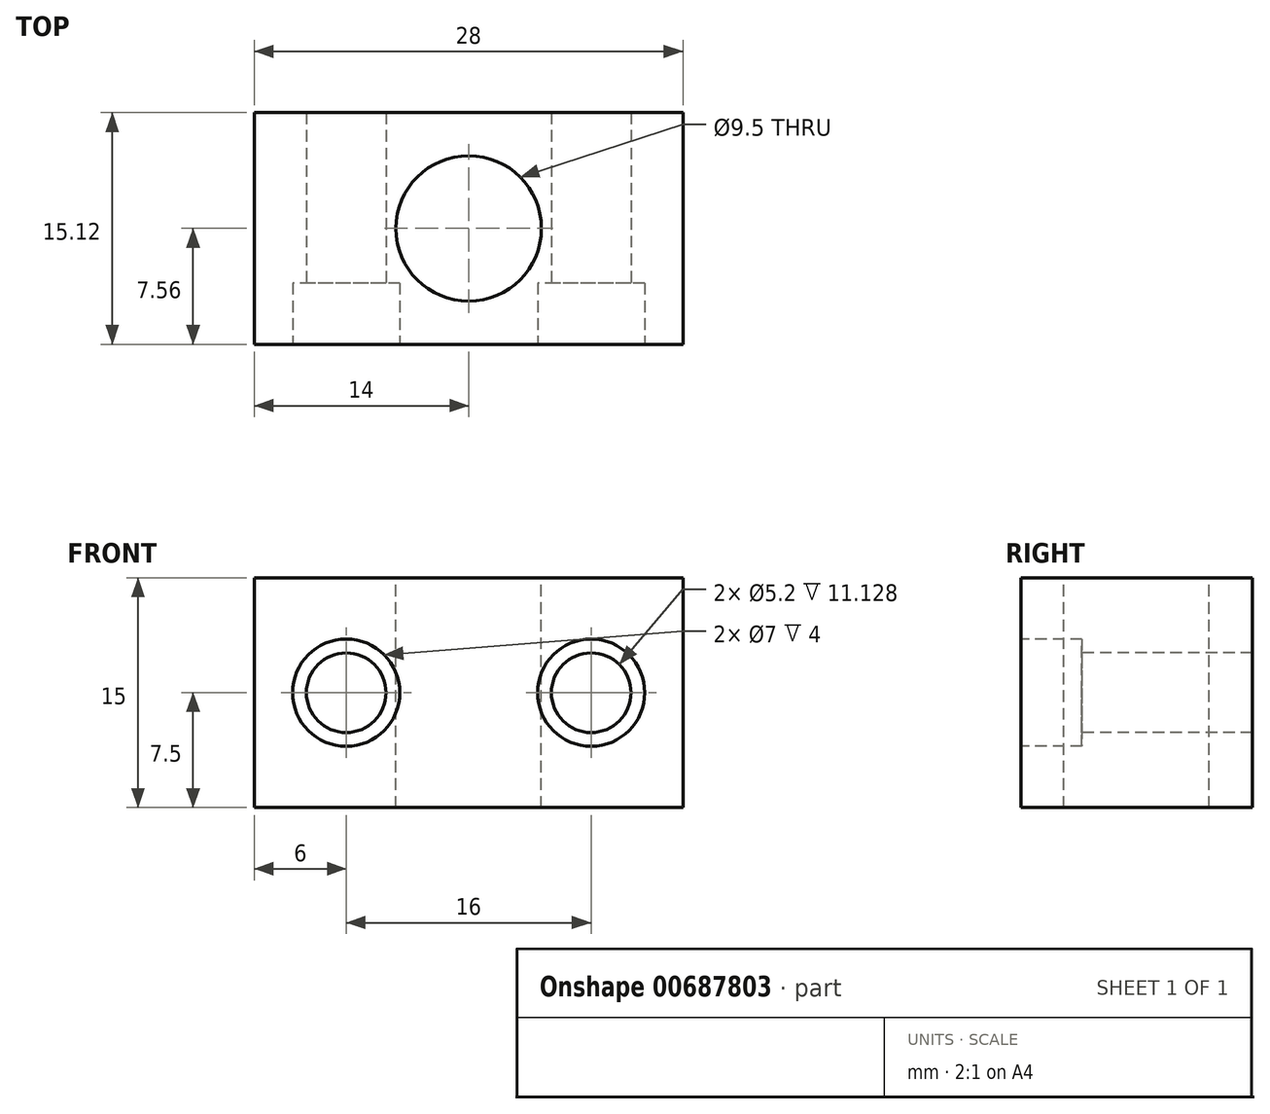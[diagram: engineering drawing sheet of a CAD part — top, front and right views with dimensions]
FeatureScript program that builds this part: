
annotation { "Feature Type Name" : "Feature", "Feature Type Description" : "" }
export const myFeature = defineFeature(function(context is Context, id is Id, definition is map)
    precondition{}
    {
        {
            var Q0;
            Q0=qCreatedBy(makeId("Top.planeOp"),FACE);
            var sketch = newSketch(context, id + "F0", { "sketchPlane" : qUnion([Q0])});
            skLineSegment(sketch, "E0.bottom", {"start": v(14, 7.56) * mm, "end": v(-14, 7.56) * mm});
            skLineSegment(sketch, "E0.top", {"start": v(14, -7.56) * mm, "end": v(-14, -7.56) * mm});
            skLineSegment(sketch, "E0.left", {"start": v(14, 7.56) * mm, "end": v(14, -7.56) * mm});
            skLineSegment(sketch, "E0.right", {"start": v(-14, 7.56) * mm, "end": v(-14, -7.56) * mm});
            skPoint(sketch, "E0.middle", {"position": v(0, 0) * mm});
            skCircle(sketch, "E1", {"center": v(0, 0) * mm, "radius": 4.75 * mm});
            skSolve(sketch);
        }
        {
            var Q0;
            Q0=makeQuery(id+"F0.imprint","IMPRINT",FACE,{"disambiguationData":[TD([[makeQuery(id+"F0.imprint","IMPRINT",EDGE,{"derivedFrom":sQuery(id+"F0.wireOp",EDGE,"E0.bottom")}),1.0]])]});
            extrude(context, id + "F1", {"entities" : qUnion([Q0]), "oppositeDirection" : true, "depth" : 15 * mm, "offsetDistance" : 25 * mm});
        }
        {
            var Q0;
            Q0=makeQuery(id+"F1.opExtrude","SWEPT_FACE",FACE,{"disambiguationData":[OSD([sQuery(id+"F0.wireOp",EDGE,"E0.top")])]});
            var sketch = newSketch(context, id + "F2", { "sketchPlane" : qUnion([Q0])});
            skCircle(sketch, "E2", {"center": v(-8, -7.5) * mm, "radius": 2.6 * mm});
            skCircle(sketch, "E3", {"center": v(8, -7.5) * mm, "radius": 2.6 * mm});
            skCircle(sketch, "E4", {"center": v(-8, -7.5) * mm, "radius": 3.5 * mm});
            skCircle(sketch, "E5", {"center": v(8, -7.5) * mm, "radius": 3.5 * mm});
            skSolve(sketch);
        }
        {
            var Q0;
            Q0=makeQuery(id+"F2.imprint","IMPRINT",FACE,{"disambiguationData":[TD([[makeQuery(id+"F2.imprint","IMPRINT",EDGE,{"derivedFrom":sQuery(id+"F2.wireOp",EDGE,"E2")}),1.0]])]});
            var Q1;
            Q1=makeQuery(id+"F2.imprint","IMPRINT",FACE,{"disambiguationData":[TD([[makeQuery(id+"F2.imprint","IMPRINT",EDGE,{"derivedFrom":sQuery(id+"F2.wireOp",EDGE,"E3")}),1.0]])]});
            extrude(context, id + "F3", {"entities" : qUnion([Q0, Q1]), "operationType" : NewBodyOperationType.REMOVE, "oppositeDirection" : true, "depth" : 25 * mm, "offsetDistance" : 25 * mm});
        }
        {
            var Q0;
            Q0=makeQuery(id+"F2.imprint","IMPRINT",FACE,{"disambiguationData":[TD([[makeQuery(id+"F2.imprint","IMPRINT",EDGE,{"derivedFrom":sQuery(id+"F2.wireOp",EDGE,"E2")}),-1.0]])]});
            var Q1;
            Q1=makeQuery(id+"F2.imprint","IMPRINT",FACE,{"disambiguationData":[TD([[makeQuery(id+"F2.imprint","IMPRINT",EDGE,{"derivedFrom":sQuery(id+"F2.wireOp",EDGE,"E3")}),-1.0]])]});
            extrude(context, id + "F4", {"entities" : qUnion([Q0, Q1]), "operationType" : NewBodyOperationType.REMOVE, "oppositeDirection" : true, "depth" : 4 * mm, "offsetDistance" : 25 * mm});
        }
    });
